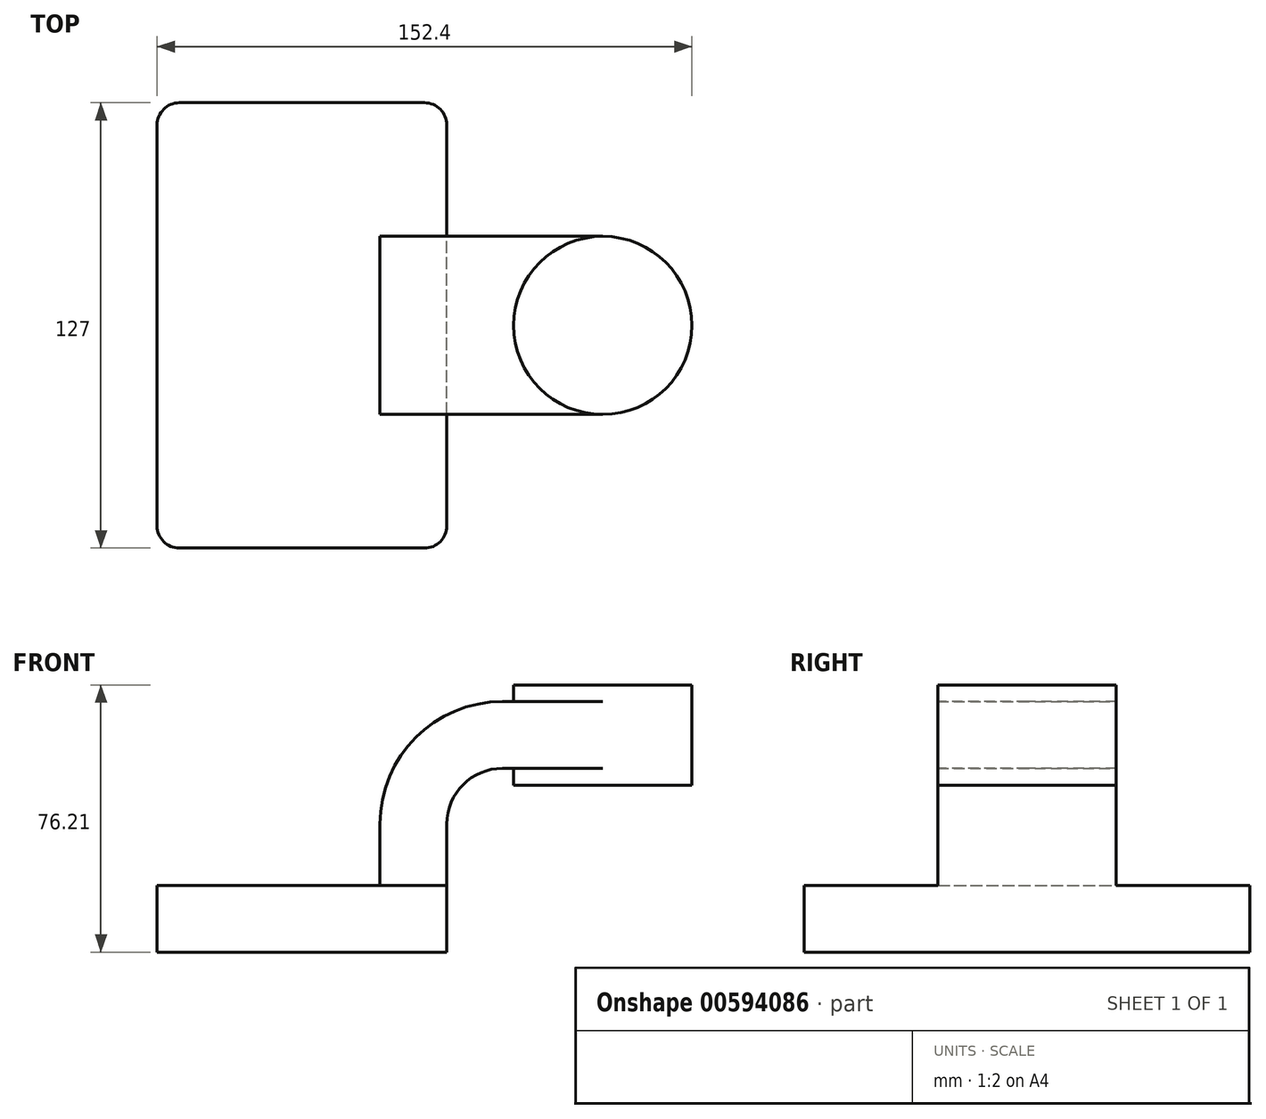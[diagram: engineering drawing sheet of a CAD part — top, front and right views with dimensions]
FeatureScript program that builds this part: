
annotation { "Feature Type Name" : "Feature", "Feature Type Description" : "" }
export const myFeature = defineFeature(function(context is Context, id is Id, definition is map)
    precondition{}
    {
        {
            var Q0;
            Q0=qCreatedBy(makeId("Front.planeOp"),FACE);
            var sketch = newSketch(context, id + "F0", { "sketchPlane" : qUnion([Q0])});
            skLineSegment(sketch, "E0.bottom", {"start": v(-41.28, 9.52) * mm, "end": v(41.28, 9.52) * mm});
            skLineSegment(sketch, "E0.top", {"start": v(-41.27, -9.53) * mm, "end": v(41.28, -9.53) * mm});
            skLineSegment(sketch, "E0.left", {"start": v(-41.27, 9.52) * mm, "end": v(-41.27, -9.53) * mm});
            skLineSegment(sketch, "E0.right", {"start": v(41.28, 9.52) * mm, "end": v(41.28, -9.53) * mm});
            skPoint(sketch, "E0.middle", {"position": v(0, 0) * mm});
            skLineSegment(sketch, "E1.bottom", {"start": v(111.12, 66.67) * mm, "end": v(60.33, 66.67) * mm});
            skLineSegment(sketch, "E1.top", {"start": v(111.12, 38.1) * mm, "end": v(60.33, 38.1) * mm});
            skLineSegment(sketch, "E1.left", {"start": v(111.13, 66.67) * mm, "end": v(111.13, 38.1) * mm});
            skLineSegment(sketch, "E1.right", {"start": v(60.33, 66.67) * mm, "end": v(60.33, 38.1) * mm});
            skPoint(sketch, "E1.middle", {"position": v(85.72, 52.39) * mm});
            skLineSegment(sketch, "E2", {"start": v(41.28, 9.52) * mm, "end": v(41.28, 27) * mm});
            skArc(sketch, "E3", {"start": v(41.28, 27) * mm, "mid": v(45.92, 38.23) * mm, "end": v(57.15, 42.88) * mm});
            skLineSegment(sketch, "E4", {"start": v(57.15, 42.88) * mm, "end": v(85.73, 42.88) * mm});
            skLineSegment(sketch, "E5.0", {"start": v(57.15, 61.93) * mm, "end": v(85.73, 61.93) * mm});
            skArc(sketch, "E5.1", {"start": v(22.23, 27) * mm, "mid": v(32.45, 51.7) * mm, "end": v(57.15, 61.93) * mm});
            skLineSegment(sketch, "E5.2", {"start": v(22.23, 9.52) * mm, "end": v(22.23, 27) * mm});
            skFitSpline(sketch, "E6", {"points": [v(-41.28, 9.52) * mm, v(57.15, 61.93) * mm], "startDerivative": vector(62.6, 65.76) * mm, "endDerivative": vector(220.92, -1.6) * mm});
            skLineSegment(sketch, "E7", {"start": v(85.72, 38.1) * mm, "end": v(85.72, 66.67) * mm});
            skSolve(sketch);
        }
        {
            var Q0;
            Q0=makeQuery(id+"F0.imprint","IMPRINT",FACE,{"disambiguationData":[TD([[makeQuery(id+"F0.imprint","IMPRINT",EDGE,{"derivedFrom":sQuery(id+"F0.wireOp",EDGE,"E0.top")}),1.0]])]});
            extrude(context, id + "F1", {"entities" : qUnion([Q0]), "endBound" : BoundingType.SYMMETRIC, "depth" : 127 * mm, "offsetDistance" : 25.4 * mm});
        }
        {
            var Q0;
            {var subQ1=sQuery(id+"F0.wireOp",EDGE,"E2");Q0=makeQuery(id+"F0.imprint","IMPRINT",FACE,{"disambiguationData":[TD([[makeQuery(id+"F0.imprint","IMPRINT",EDGE,{"derivedFrom":subQ1}),1.0]])]});}
            var Q1;
            {var subQ0=sQuery(id+"F0.wireOp",EDGE,"E5.0");var subQ1=sQuery(id+"F0.wireOp",EDGE,"E1.right");var subQ2=makeQuery(id+"F0.imprint","INTERSECT",VERTEX,{"derivedFrom":[subQ1,subQ0]});Q1=makeQuery(id+"F0.imprint","IMPRINT",FACE,{"disambiguationData":[TD([[makeQuery(id+"F0.imprint","IMPRINT",EDGE,{"disambiguationData":[TD([[subQ2,-1.0]])],"derivedFrom":subQ1}),1.0]])]});}
            extrude(context, id + "F2", {"entities" : qUnion([Q0, Q1]), "operationType" : NewBodyOperationType.ADD, "endBound" : BoundingType.SYMMETRIC, "depth" : 50.8 * mm, "offsetDistance" : 25.4 * mm});
        }
        {
            var Q0;
            Q0=makeQuery(id+"F0.imprint","IMPRINT",FACE,{"disambiguationData":[TD([[makeQuery(id+"F0.imprint","IMPRINT",EDGE,{"derivedFrom":sQuery(id+"F0.wireOp",EDGE,"E5.1")}),1.0]])]});
            extrude(context, id + "F3", {"entities" : qUnion([Q0]), "operationType" : NewBodyOperationType.ADD, "endBound" : BoundingType.SYMMETRIC, "depth" : 15.88 * mm, "offsetDistance" : 25.4 * mm});
        }
        {
            var Q0;
            {var subQ0=sQuery(id+"F0.wireOp",EDGE,"E1.left");Q0=makeQuery(id+"F0.imprint","IMPRINT",FACE,{"disambiguationData":[TD([[makeQuery(id+"F0.imprint","IMPRINT",EDGE,{"derivedFrom":subQ0}),-1.0]])]});}
            var Q1;
            Q1=sQuery(id+"F0.wireOp",EDGE,"E7");
            revolve(context, id + "F4", {"operationType" : NewBodyOperationType.ADD, "entities" : qUnion([Q0]), "axis" : qUnion([Q1]), "revolveType" : RevolveType.FULL});
        }
        {
            var Q0;
            Q0=makeQuery(id+"F1.opExtrude","CAP_EDGE",EDGE,{"disambiguationData":[OSD([sQuery(id+"F0.wireOp",EDGE,"E0.right")])],"isStart":false});
            var Q1;
            Q1=makeQuery(id+"F1.opExtrude","CAP_EDGE",EDGE,{"disambiguationData":[OSD([sQuery(id+"F0.wireOp",EDGE,"E0.left")])],"isStart":false});
            var Q2;
            Q2=makeQuery(id+"F1.opExtrude","CAP_EDGE",EDGE,{"disambiguationData":[OSD([sQuery(id+"F0.wireOp",EDGE,"E0.right")])],"isStart":true});
            var Q3;
            Q3=makeQuery(id+"F1.opExtrude","CAP_EDGE",EDGE,{"disambiguationData":[OSD([sQuery(id+"F0.wireOp",EDGE,"E0.left")])],"isStart":true});
            fillet(context, id + "F5", {"entities" : qUnion([Q0, Q1, Q2, Q3]), "radius" : 6.35 * mm, "tangentPropagation" : true, "allowEdgeOverflow" : false});
        }
    });
